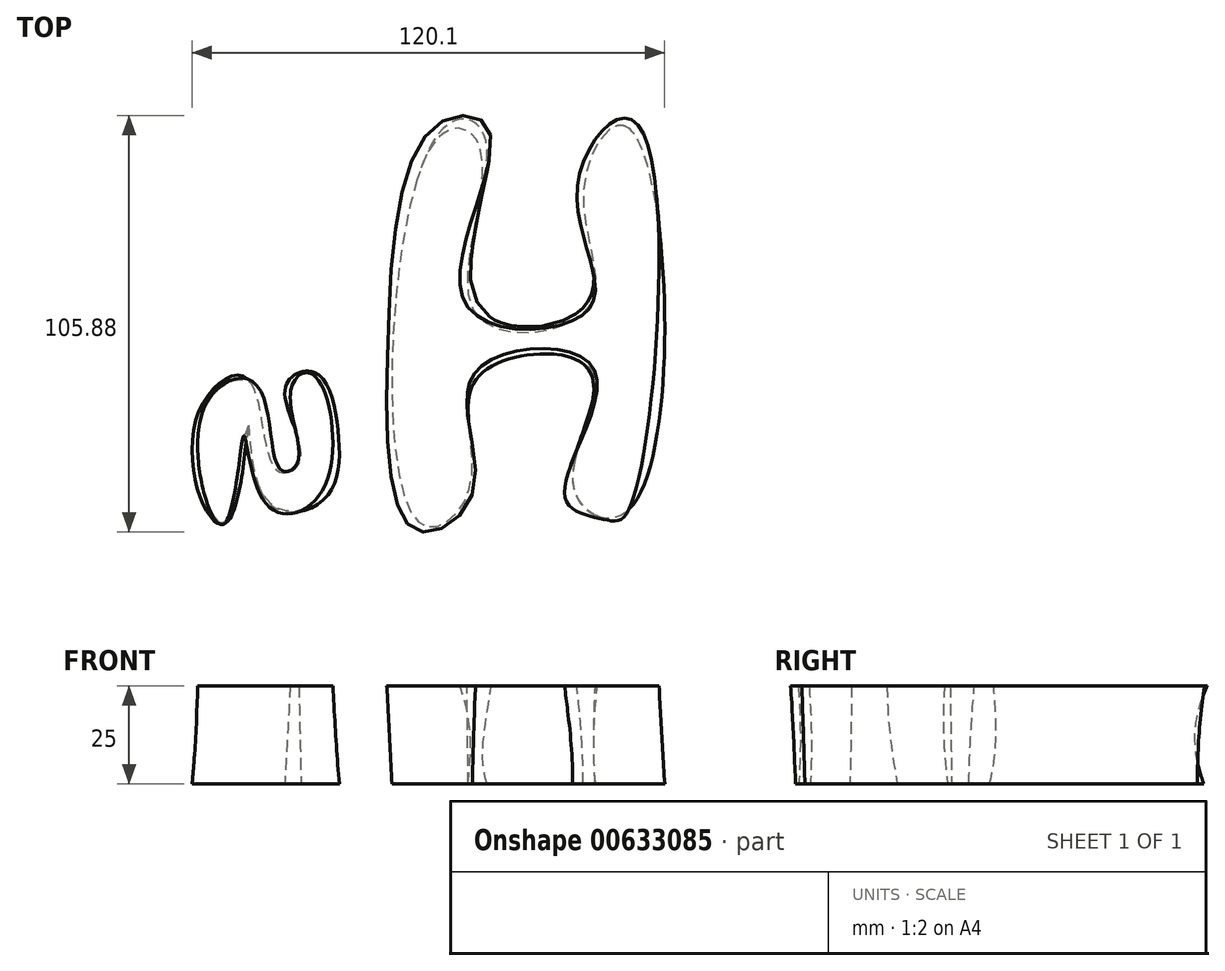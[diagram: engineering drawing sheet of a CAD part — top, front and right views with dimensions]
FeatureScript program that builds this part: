
annotation { "Feature Type Name" : "Feature", "Feature Type Description" : "" }
export const myFeature = defineFeature(function(context is Context, id is Id, definition is map)
    precondition{}
    {
        {
            var Q0;
            Q0=qCreatedBy(makeId("Top.planeOp"),FACE);
            var sketch = newSketch(context, id + "F0", { "sketchPlane" : qUnion([Q0])});
            skFitSpline(sketch, "E0", {"points": [v(58.6, -45.76) * mm, v(58.29, 50.58) * mm, v(46.73, 35.49) * mm, v(47.7, 4.66) * mm, v(19.43, 3.37) * mm, v(21.68, 48.33) * mm, v(10.12, 49.62) * mm, v(4.66, -49.3) * mm, v(17.82, -40.62) * mm, v(20.07, -12.36) * mm, v(48.65, -10.76) * mm, v(44.16, -40.62) * mm, v(58.6, -45.76) * mm]});
            skFitSpline(sketch, "E1", {"points": [v(-37.41, 19.1) * mm, v(-20.4, 17.82) * mm, v(-20.4, 49.62) * mm, v(-32.92, 40.95) * mm, v(-36.45, 33.56) * mm, v(-40.3, 48.97) * mm, v(-45.76, 47.7) * mm, v(-37.41, 19.1) * mm]});
            skSolve(sketch);
        }
        {
            var Q0;
            Q0=qCreatedBy(makeId("Top.planeOp"),FACE);
            cPlane(context, id + "F1", {"entities" : qUnion([Q0]), "cplaneType" : CPlaneType.OFFSET, "offset" : 25 * mm, "width" : 150 * mm, "height" : 150 * mm});
        }
        {
            var Q0;
            Q0=qCreatedBy(id+"F1.planeOp",FACE);
            var sketch = newSketch(context, id + "F2", { "sketchPlane" : qUnion([Q0])});
            skFitSpline(sketch, "E2", {"points": [v(58.29, -46.08) * mm, v(51.54, -48.65) * mm, v(41.9, -42.55) * mm, v(49.3, -10.44) * mm, v(19.43, -11.08) * mm, v(18.79, -41.27) * mm, v(4.34, -51.54) * mm, v(-3.05, -4.98) * mm, v(9.47, 51.54) * mm, v(22.96, 49.62) * mm, v(16.86, 5.94) * mm, v(48.01, 4.66) * mm, v(45.12, 35.8) * mm, v(59.9, 52.19) * mm, v(58.29, -46.08) * mm]});
            skFitSpline(sketch, "E3", {"points": [v(-43.84, 50.9) * mm, v(-47.05, 46.73) * mm, v(-36.45, 15.25) * mm, v(-20.71, 18.47) * mm, v(-20.07, 50.58) * mm, v(-36.45, 34.84) * mm, v(-39.02, 46.73) * mm, v(-43.84, 50.9) * mm]});
            skSolve(sketch);
        }
        {
            var Q0;
            Q0=makeQuery(id+"F2.imprint","IMPRINT",FACE,{"disambiguationData":[TD([[makeQuery(id+"F2.imprint","IMPRINT",EDGE,{"derivedFrom":sQuery(id+"F2.wireOp",EDGE,"E2")}),-1.0]])]});
            var Q1;
            Q1=makeQuery(id+"F0.imprint","IMPRINT",FACE,{"disambiguationData":[TD([[makeQuery(id+"F0.imprint","IMPRINT",EDGE,{"derivedFrom":sQuery(id+"F0.wireOp",EDGE,"E0")}),1.0]])]});
            loft(context, id + "F3", {"sheetProfilesArray" : [{ "sheetProfileEntities" : qUnion([Q0]) }, { "sheetProfileEntities" : qUnion([Q1]) }]});
        }
        {
            var Q0;
            Q0=qCreatedBy(id+"F1.planeOp",FACE);
            var sketch = newSketch(context, id + "F4", { "sketchPlane" : qUnion([Q0])});
            skFitSpline(sketch, "E4", {"points": [v(-39.61, -27.54) * mm, v(-33.81, -44.9) * mm, v(-19.3, -40.73) * mm, v(-22.15, -11.88) * mm, v(-27.63, -15.75) * mm, v(-25.9, -34.13) * mm, v(-30.36, -35.96) * mm, v(-36.57, -14.33) * mm, v(-50.28, -21.96) * mm, v(-44.68, -49.89) * mm, v(-39.61, -27.54) * mm]});
            skSolve(sketch);
        }
        {
            var Q0;
            Q0=qCreatedBy(makeId("Top.planeOp"),FACE);
            var sketch = newSketch(context, id + "F5", { "sketchPlane" : qUnion([Q0])});
            skFitSpline(sketch, "E5", {"points": [v(-21.68, -11.4) * mm, v(-15.58, -26.82) * mm, v(-19.43, -43.84) * mm, v(-33.88, -43.84) * mm, v(-38.38, -24.89) * mm, v(-43.2, -48.65) * mm, v(-48.33, -47.7) * mm, v(-50.9, -21.04) * mm, v(-38.7, -13) * mm, v(-31.31, -36.13) * mm, v(-25.2, -33.56) * mm, v(-29.06, -15.25) * mm, v(-21.68, -11.4) * mm]});
            skSolve(sketch);
        }
        {
            var Q0;
            Q0=makeQuery(id+"F5.imprint","IMPRINT",FACE,{"disambiguationData":[TD([[makeQuery(id+"F5.imprint","IMPRINT",EDGE,{"derivedFrom":sQuery(id+"F5.wireOp",EDGE,"E5")}),-1.0]])]});
            var Q1;
            Q1=makeQuery(id+"F4.imprint","IMPRINT",FACE,{"disambiguationData":[TD([[makeQuery(id+"F4.imprint","IMPRINT",EDGE,{"derivedFrom":sQuery(id+"F4.wireOp",EDGE,"E4")}),1.0]])]});
            loft(context, id + "F6", {"sheetProfilesArray" : [{ "sheetProfileEntities" : qUnion([Q0]) }, { "sheetProfileEntities" : qUnion([Q1]) }]});
        }
    });
